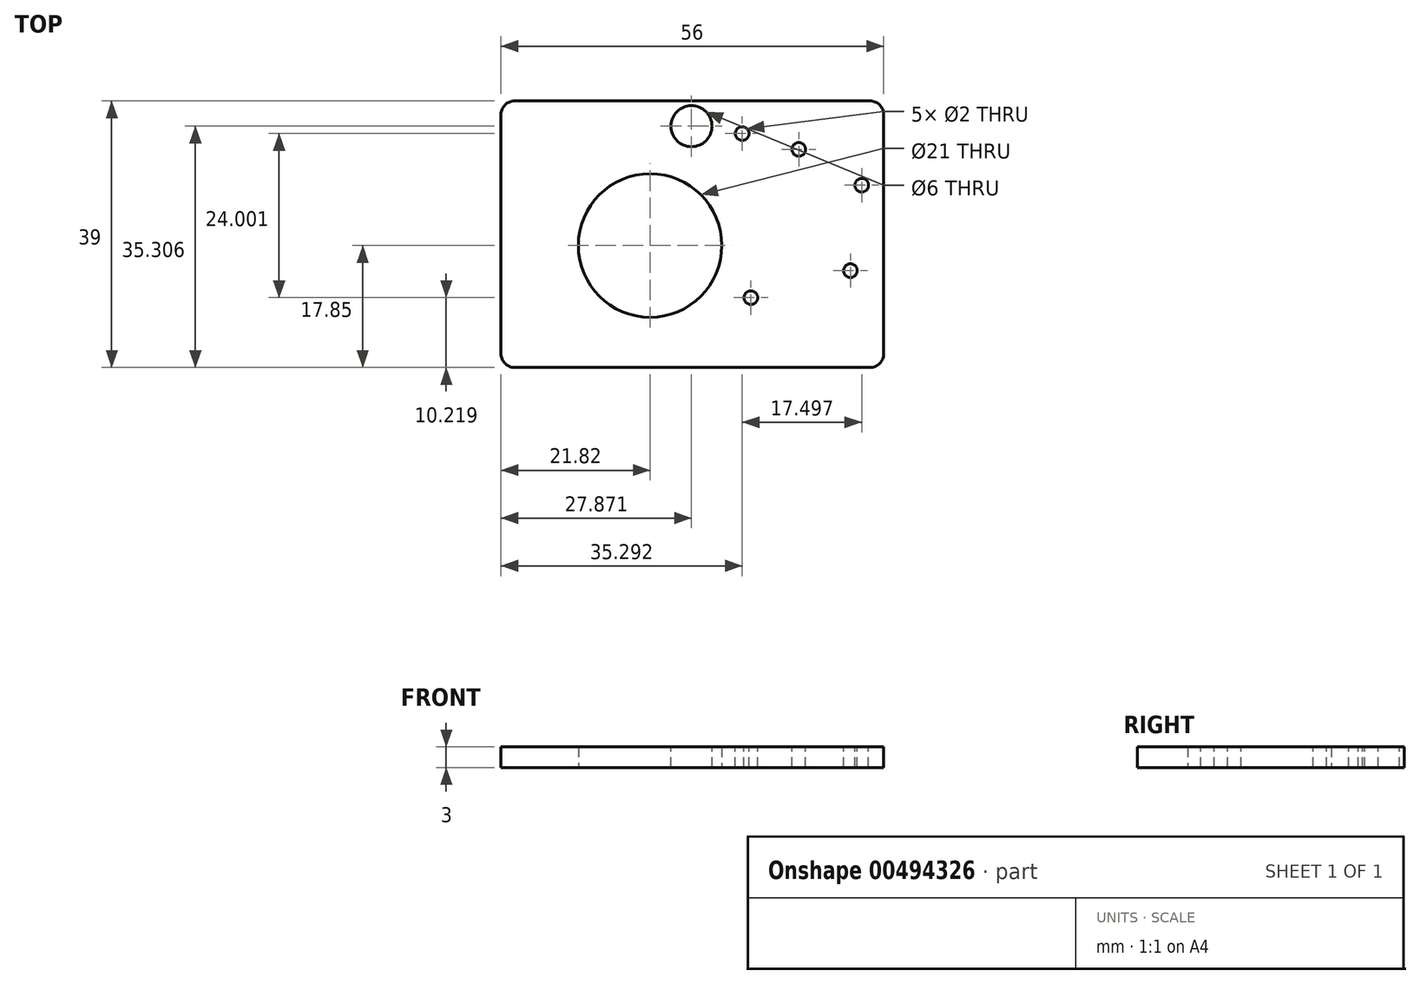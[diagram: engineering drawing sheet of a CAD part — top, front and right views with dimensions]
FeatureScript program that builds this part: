
annotation { "Feature Type Name" : "Feature", "Feature Type Description" : "" }
export const myFeature = defineFeature(function(context is Context, id is Id, definition is map)
    precondition{}
    {
        {
            var Q0;
            Q0=qCreatedBy(makeId("Top.planeOp"),FACE);
            var sketch = newSketch(context, id + "F0", { "sketchPlane" : qUnion([Q0])});
            skLineSegment(sketch, "E0.bottom", {"start": v(34.18, 21.15) * mm, "end": v(-21.82, 21.15) * mm});
            skLineSegment(sketch, "E0.top", {"start": v(34.18, -17.85) * mm, "end": v(-21.82, -17.85) * mm});
            skLineSegment(sketch, "E0.left", {"start": v(34.18, 21.15) * mm, "end": v(34.18, -17.85) * mm});
            skLineSegment(sketch, "E0.right", {"start": v(-21.82, 21.15) * mm, "end": v(-21.82, -17.85) * mm});
            skPoint(sketch, "E0.middle", {"position": v(0, 0) * mm});
            skCircle(sketch, "E1", {"center": v(0, 0) * mm, "radius": 10.5 * mm});
            skSolve(sketch);
        }
        {
            var Q0;
            Q0=makeQuery(id+"F0.imprint","IMPRINT",FACE,{"disambiguationData":[TD([[makeQuery(id+"F0.imprint","IMPRINT",EDGE,{"derivedFrom":sQuery(id+"F0.wireOp",EDGE,"E0.bottom")}),1.0]])]});
            extrude(context, id + "F1", {"entities" : qUnion([Q0]), "depth" : 3 * mm});
        }
        {
            var Q0;
            Q0=makeQuery(id+"F1.opExtrude","SWEPT_EDGE",EDGE,{"disambiguationData":[OSD([sQuery(id+"F0.wireOp",EDGE,"E0.top"),sQuery(id+"F0.wireOp",EDGE,"E0.right")])]});
            var Q1;
            Q1=makeQuery(id+"F1.opExtrude","SWEPT_EDGE",EDGE,{"disambiguationData":[OSD([sQuery(id+"F0.wireOp",EDGE,"E0.top"),sQuery(id+"F0.wireOp",EDGE,"E0.left")])]});
            var Q2;
            Q2=makeQuery(id+"F1.opExtrude","SWEPT_EDGE",EDGE,{"disambiguationData":[OSD([sQuery(id+"F0.wireOp",EDGE,"E0.bottom"),sQuery(id+"F0.wireOp",EDGE,"E0.left")])]});
            var Q3;
            Q3=makeQuery(id+"F1.opExtrude","SWEPT_EDGE",EDGE,{"disambiguationData":[OSD([sQuery(id+"F0.wireOp",EDGE,"E0.bottom"),sQuery(id+"F0.wireOp",EDGE,"E0.right")])]});
            fillet(context, id + "F2", {"entities" : qUnion([Q0, Q1, Q2, Q3]), "radius" : 2 * mm, "tangentPropagation" : true, "allowEdgeOverflow" : false});
        }
        {
            var Q0;
            Q0=makeQuery(id+"F1.opExtrude","CAP_FACE",FACE,{"disambiguationData":[OSD([sQuery(id+"F0.wireOp",EDGE,"E0.bottom"),sQuery(id+"F0.wireOp",EDGE,"E0.top"),sQuery(id+"F0.wireOp",EDGE,"E0.left"),sQuery(id+"F0.wireOp",EDGE,"E0.right"),sQuery(id+"F0.wireOp",EDGE,"E1"),sQuery(id+"F0.wireOp",EDGE,"kD9CTKkK-tv1s-ftBN-gvyZ-TyXxSfsiQNbb.bottom"),sQuery(id+"F0.wireOp",EDGE,"kD9CTKkK-tv1s-ftBN-gvyZ-TyXxSfsiQNbb.top"),sQuery(id+"F0.wireOp",EDGE,"kD9CTKkK-tv1s-ftBN-gvyZ-TyXxSfsiQNbb.left")])],"isStart":false});
            var sketch = newSketch(context, id + "F3", { "sketchPlane" : qUnion([Q0])});
            skCircle(sketch, "E2", {"center": v(0, 0) * mm, "radius": 14 * mm});
            skCircle(sketch, "E3", {"center": v(14.74, -7.63) * mm, "radius": 2.6 * mm, "construction": true});
            skCircle(sketch, "E4", {"center": v(14.74, -7.63) * mm, "radius": 12.5 * mm, "construction": true});
            skCircle(sketch, "E5", {"center": v(29.31, -3.67) * mm, "radius": 2.6 * mm, "construction": true});
            skCircle(sketch, "E6", {"center": v(29.31, -3.67) * mm, "radius": 10 * mm, "construction": true});
            skCircle(sketch, "E7", {"center": v(30.97, 8.82) * mm, "radius": 2.6 * mm, "construction": true});
            skCircle(sketch, "E8", {"center": v(30.97, 8.82) * mm, "radius": 8.5 * mm, "construction": true});
            skCircle(sketch, "E9", {"center": v(21.76, 14.06) * mm, "radius": 2.1 * mm, "construction": true});
            skCircle(sketch, "E10", {"center": v(21.76, 14.06) * mm, "radius": 6.5 * mm, "construction": true});
            skCircle(sketch, "E11", {"center": v(13.47, 16.37) * mm, "radius": 5 * mm, "construction": true});
            skCircle(sketch, "E12", {"center": v(14.74, -7.63) * mm, "radius": 13 * mm, "construction": true});
            skCircle(sketch, "E13", {"center": v(29.31, -3.67) * mm, "radius": 10.5 * mm, "construction": true});
            skCircle(sketch, "E14", {"center": v(30.97, 8.82) * mm, "radius": 9 * mm, "construction": true});
            skCircle(sketch, "E15", {"center": v(21.76, 14.06) * mm, "radius": 7 * mm, "construction": true});
            skCircle(sketch, "E16", {"center": v(13.47, 16.37) * mm, "radius": 5.5 * mm, "construction": true});
            skCircle(sketch, "E17", {"center": v(30.97, 8.82) * mm, "radius": 1 * mm});
            skCircle(sketch, "E18", {"center": v(21.76, 14.06) * mm, "radius": 1 * mm});
            skCircle(sketch, "E19", {"center": v(13.47, 16.37) * mm, "radius": 1 * mm});
            skCircle(sketch, "E20", {"center": v(29.31, -3.67) * mm, "radius": 1 * mm});
            skCircle(sketch, "E21", {"center": v(14.74, -7.63) * mm, "radius": 1 * mm});
            skCircle(sketch, "E22", {"center": v(6.05, 17.46) * mm, "radius": 2.5 * mm, "construction": true});
            skCircle(sketch, "E23", {"center": v(6.05, 17.46) * mm, "radius": 3 * mm});
            skCircle(sketch, "E24", {"center": v(13.47, 16.37) * mm, "radius": 2.1 * mm, "construction": true});
            skSolve(sketch);
        }
        {
            var Q0;
            Q0=makeQuery(id+"F3.imprint","IMPRINT",FACE,{"disambiguationData":[TD([[makeQuery(id+"F3.imprint","IMPRINT",EDGE,{"derivedFrom":sQuery(id+"F3.wireOp",EDGE,"E20")}),1.0]])]});
            var Q1;
            Q1=makeQuery(id+"F3.imprint","IMPRINT",FACE,{"disambiguationData":[TD([[makeQuery(id+"F3.imprint","IMPRINT",EDGE,{"derivedFrom":sQuery(id+"F3.wireOp",EDGE,"E21")}),1.0]])]});
            var Q2;
            Q2=makeQuery(id+"F3.imprint","IMPRINT",FACE,{"disambiguationData":[TD([[makeQuery(id+"F3.imprint","IMPRINT",EDGE,{"derivedFrom":sQuery(id+"F3.wireOp",EDGE,"E17")}),1.0]])]});
            var Q3;
            Q3=makeQuery(id+"F3.imprint","IMPRINT",FACE,{"disambiguationData":[TD([[makeQuery(id+"F3.imprint","IMPRINT",EDGE,{"derivedFrom":sQuery(id+"F3.wireOp",EDGE,"E18")}),1.0]])]});
            var Q4;
            Q4=makeQuery(id+"F3.imprint","IMPRINT",FACE,{"disambiguationData":[TD([[makeQuery(id+"F3.imprint","IMPRINT",EDGE,{"derivedFrom":sQuery(id+"F3.wireOp",EDGE,"E19")}),1.0]])]});
            var Q5;
            Q5=makeQuery(id+"F3.imprint","IMPRINT",FACE,{"disambiguationData":[TD([[makeQuery(id+"F3.imprint","IMPRINT",EDGE,{"derivedFrom":sQuery(id+"F3.wireOp",EDGE,"E23")}),1.0]])]});
            extrude(context, id + "F4", {"entities" : qUnion([Q0, Q1, Q2, Q3, Q4, Q5]), "operationType" : NewBodyOperationType.REMOVE, "endBound" : BoundingType.UP_TO_NEXT, "oppositeDirection" : true, "depth" : 25 * mm});
        }
    });
